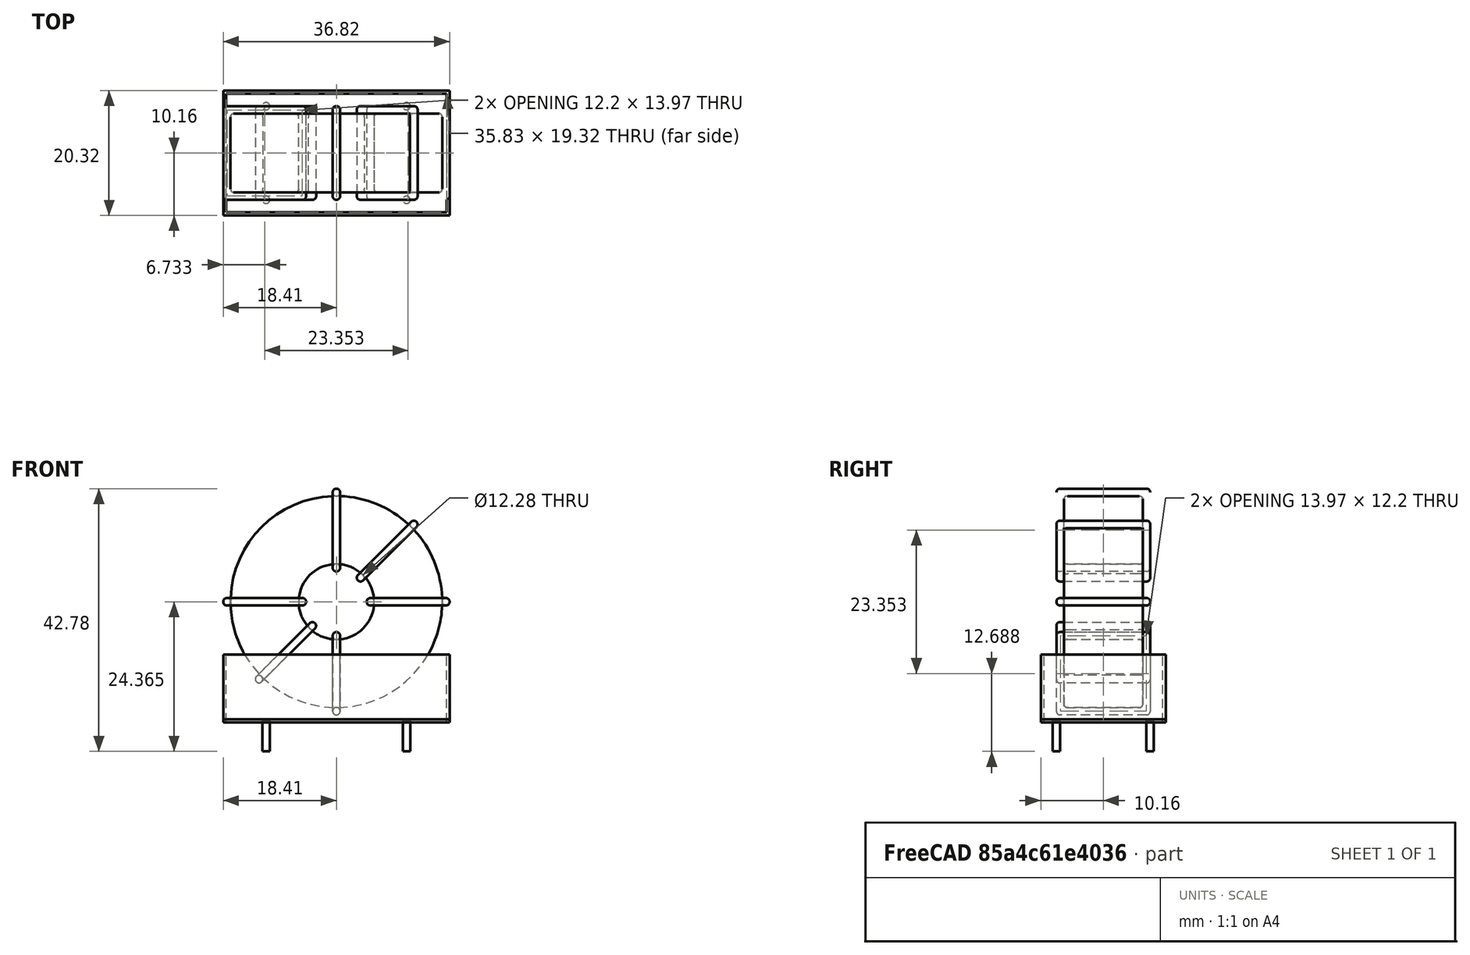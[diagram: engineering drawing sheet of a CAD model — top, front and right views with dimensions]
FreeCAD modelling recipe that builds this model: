
FCSTD DOCUMENT  (FreeCAD 0.16R6703 (Git))
Label: L_CommonModeChoke_Toroid_Vertical_L36.8mm_W20.3mm_Px15.24mm_Py22.86mm_Bourns_8100series
License: All rights reserved
LicenseURL: http://en.wikipedia.org/wiki/All_rights_reserved
objects: Sketcher::SketchObject×8, PartDesign::Pad×8, PartDesign::Fillet×5, Spreadsheet::Sheet×1
note: 29 computed .brp shape members not serialized (recipe doc carries the construction recipe); baked Part::Feature solids carry a one-line shape summary decoded from their .brp

FEATURE [Spreadsheet::Sheet] Spreadsheet  label="dimensions"
  cells = A1=Wx; B1(Wx)=36.83; C1(WW)=12.27666666666667; D1(iWx)=36.83; A2=Wy; B2(Wy)=15.24; D2(iWy)=20.32; A3=RM; B3(RMx)=15.24; C3(RMy)=22.86; A4=d_wire; B4(d_wire)=1.2; A5=H; B5(H)=31; A6=offsetx; B6(offsetx)=6.984999999999999
FEATURE [Sketcher::SketchObject] Sketch
  Placement = pos=(11.43,-7.62,0) rot=(1,0,0;1.5708rad)
  expr: Placement.Base.x = Spreadsheet.RMy / 2
  expr: Constraints[4] = Spreadsheet.WW / 2
  expr: Placement.Base.y = -Spreadsheet.RMx / 2
  expr: Constraints[0] = Spreadsheet.Wx / 2 - Spreadsheet.d_wire
  expr: Constraints[2] = Spreadsheet.Wx / 2 + Spreadsheet.d_wire + 0.5
  sketch-geometry (2):
    g0: Circle CenterX=0 CenterY=20.115 CenterZ=0 NormalX=0 NormalY=0 NormalZ=1 Radius=17.215
    g1: Circle CenterX=0 CenterY=20.115 CenterZ=0 NormalX=0 NormalY=0 NormalZ=1 Radius=6.13833
  constraints (5):
    c: Radius(g0) = 17.215
    c: DistanceX(g-1,g0) = 0
    c: DistanceY(g-1,g0) = 20.115
    c: Coincident(g1,g0)
    c: Radius(g1) = 6.13833
FEATURE [PartDesign::Pad] Pad
  Length = 12.84
  Length2 = 100
  Midplane = true
  Placement = pos=(11.43,-7.62,0) rot=(1,0,0;1.5708rad)
  Sketch = -> Sketch
  Type = 0
  expr: Length = Spreadsheet.Wy - 2 * Spreadsheet.d_wire
FEATURE [Sketcher::SketchObject] Sketch001
  Placement = pos=(0,0,0.75) rot=(0,0,1;0rad)
  expr: Constraints[4] = Spreadsheet.RMy
  expr: Constraints[2] = -Spreadsheet.RMx
  expr: Constraints[1] = Spreadsheet.d_wire / 2
  sketch-geometry (4):
    g0: Circle CenterX=0 CenterY=0 CenterZ=0 NormalX=0 NormalY=0 NormalZ=1 Radius=0.6
    g1: Circle CenterX=22.86 CenterY=-15.24 CenterZ=0 NormalX=0 NormalY=0 NormalZ=1 Radius=0.6
    g2: Circle CenterX=0 CenterY=-15.24 CenterZ=0 NormalX=0 NormalY=0 NormalZ=1 Radius=0.6
    g3: Circle CenterX=22.86 CenterY=0 CenterZ=0 NormalX=0 NormalY=0 NormalZ=1 Radius=0.6
  constraints (11):
    c: Equal(g0,g1)
    c: Radius(g0) = 0.6
    c: DistanceY(g-1,g1) = -15.24
    c: Coincident(g0,g-1)
    c: DistanceX(g-1,g1) = 22.86
    c: PointOnObject(g2,g-2)
    c: DistanceY(g-1,g3) = 0
    c: DistanceY(g2,g1) = 0
    c: DistanceX(g3,g1) = 0
    c: Equal(g3,g2)
    c: Equal(g2,g1)
FEATURE [PartDesign::Pad] Pad001
  Length = 5
  Length2 = 0
  Placement = pos=(0,0,0.75) rot=(0,0,1;0rad)
  Reversed = true
  Sketch = -> Sketch001
  Type = 0
FEATURE [PartDesign::Fillet] Fillet
  Base = -> Pad [Edge6,Edge3,Edge2]
  Placement = pos=(11.43,-7.62,0) rot=(1,0,0;1.5708rad)
  Radius = 0.5
FEATURE [Sketcher::SketchObject] Sketch003
  Placement = pos=(11.43,0,20.115) rot=(1,0,0;3.14159rad)
  expr: Placement.Base.x = Spreadsheet.RMy / 2
  expr: Constraints[18] = Spreadsheet.d_wire
  expr: Constraints[16] = Spreadsheet.d_wire
  expr: Constraints[19] = Spreadsheet.d_wire
  expr: Constraints[17] = Spreadsheet.d_wire
  expr: Placement.Base.y = -1 * (Spreadsheet.RMx - Spreadsheet.Wy) / 2
  expr: Constraints[21] = (Spreadsheet.Wx - Spreadsheet.WW) / 2 - Spreadsheet.d_wire
  expr: Constraints[22] = Spreadsheet.Wx / 2 - Spreadsheet.d_wire
  expr: Constraints[43] = Spreadsheet.d_wire
  expr: Constraints[48] = Spreadsheet.Wx - Spreadsheet.d_wire * 2
  expr: Constraints[49] = Spreadsheet.Wy
  expr: Placement.Base.z = Spreadsheet.Wx / 2 + Spreadsheet.d_wire + 0.5
  sketch-geometry (16):
    g0: LineSegment StartX=-4.93833 StartY=0 StartZ=0 EndX=-18.415 EndY=0 EndZ=0
    g1: LineSegment StartX=-18.415 StartY=0 StartZ=0 EndX=-18.415 EndY=15.24 EndZ=0
    g2: LineSegment StartX=-18.415 StartY=15.24 StartZ=0 EndX=-4.93833 EndY=15.24 EndZ=0
    g3: LineSegment StartX=-4.93833 StartY=15.24 StartZ=0 EndX=-4.93833 EndY=0 EndZ=0
    g4: LineSegment StartX=-17.215 StartY=14.04 StartZ=0 EndX=-6.13833 EndY=14.04 EndZ=0
    g5: LineSegment StartX=-6.13833 StartY=14.04 StartZ=0 EndX=-6.13833 EndY=1.2 EndZ=0
    g6: LineSegment StartX=-6.13833 StartY=1.2 StartZ=0 EndX=-17.215 EndY=1.2 EndZ=0
    g7: LineSegment StartX=-17.215 StartY=1.2 StartZ=0 EndX=-17.215 EndY=14.04 EndZ=0
    g8: LineSegment StartX=4.93833 StartY=15.24 StartZ=0 EndX=18.415 EndY=15.24 EndZ=0
    g9: LineSegment StartX=18.415 StartY=15.24 StartZ=0 EndX=18.415 EndY=0 EndZ=0
    g10: LineSegment StartX=18.415 StartY=0 StartZ=0 EndX=4.93833 EndY=0 EndZ=0
    g11: LineSegment StartX=4.93833 StartY=0 StartZ=0 EndX=4.93833 EndY=15.24 EndZ=0
    g12: LineSegment StartX=6.13833 StartY=14.04 StartZ=0 EndX=17.215 EndY=14.04 EndZ=0
    g13: LineSegment StartX=17.215 StartY=14.04 StartZ=0 EndX=17.215 EndY=1.2 EndZ=0
    g14: LineSegment StartX=17.215 StartY=1.2 StartZ=0 EndX=6.13833 EndY=1.2 EndZ=0
    g15: LineSegment StartX=6.13833 StartY=1.2 StartZ=0 EndX=6.13833 EndY=14.04 EndZ=0
  constraints (50):
    c: Horizontal(g0)
    c: Coincident(g1,g0)
    c: Vertical(g1)
    c: Coincident(g2,g1)
    c: Horizontal(g2)
    c: Coincident(g3,g2)
    c: Coincident(g3,g0)
    c: Vertical(g3)
    c: Coincident(g4,g5)
    c: Coincident(g5,g6)
    c: Coincident(g6,g7)
    c: Coincident(g7,g4)
    c: Horizontal(g4)
    c: Horizontal(g6)
    c: Vertical(g5)
    c: Vertical(g7)
    c: DistanceX(g1,g4) = 1.2
    c: DistanceY(g4,g1) = 1.2
    c: DistanceX(g5,g0) = 1.2
    c: DistanceY(g0,g5) = 1.2
    c: DistanceY(g-1,g0) = 0
    c: DistanceX(g6,g6) = 11.0767
    c: DistanceX(g6,g-1) = 17.215
    c: Coincident(g8,g9)
    c: Coincident(g9,g10)
    c: Coincident(g10,g11)
    c: Coincident(g11,g8)
    c: Horizontal(g8)
    c: Horizontal(g10)
    c: Vertical(g9)
    c: Vertical(g11)
    c: Coincident(g12,g13)
    c: Coincident(g13,g14)
    c: Coincident(g14,g15)
    c: Coincident(g15,g12)
    c: Horizontal(g12)
    c: Horizontal(g14)
    c: Vertical(g13)
    c: Vertical(g15)
    c: DistanceY(g8,g2) = 0
    c: DistanceY(g10,g0) = 0
    c: DistanceY(g14,g5) = 0
    c: DistanceY(g12,g4) = 0
    c: DistanceX(g8,g12) = 1.2
    c: Equal(g8,g2)
    c: Equal(g12,g4)
    c: Equal(g9,g1)
    c: Equal(g13,g7)
    c: DistanceX(g4,g12) = 34.43
    c: DistanceY(g0,g1) = 15.24
FEATURE [PartDesign::Pad] Pad002
  Length = 1.2
  Length2 = 100
  Midplane = true
  Placement = pos=(11.43,0,20.115) rot=(1,0,0;3.14159rad)
  Sketch = -> Sketch003
  Type = 0
  expr: Length = Spreadsheet.d_wire
FEATURE [PartDesign::Fillet] Fillet001
  Base = -> Pad002 [Edge38,Edge41,Edge42,Edge43,Edge29,Edge32,Edge33,Edge34,Edge25,Edge35,Edge36,Edge13,Edge14,Edge15,Edge16,Edge17,Edge18,Edge19,Edge1,Edge2,Edge3,Edge4,Edge5,Edge6,Edge7,Edge37,Edge39,Edge40,Edge20,Edge23,Edge24,Edge21,Edge22,Edge8,Edge9,Edge10,Edge11,Edge12,Edge26,Edge27,+8 more]
  Placement = pos=(11.43,0,20.115) rot=(1,0,0;3.14159rad)
  Radius = 0.564
  expr: Radius = Spreadsheet.d_wire * 0.47
FEATURE [Sketcher::SketchObject] Sketch004
  Placement = pos=(11.43,0,20.115) rot=(0.92388,0,0.382683;3.14159rad)
  expr: Placement.Base.x = Spreadsheet.RMy / 2
  expr: Constraints[18] = Spreadsheet.d_wire
  expr: Constraints[16] = Spreadsheet.d_wire
  expr: Constraints[19] = Spreadsheet.d_wire
  expr: Constraints[17] = Spreadsheet.d_wire
  expr: Placement.Base.y = -1 * (Spreadsheet.RMx - Spreadsheet.Wy) / 2
  expr: Constraints[21] = (Spreadsheet.Wx - Spreadsheet.WW) / 2 - Spreadsheet.d_wire
  expr: Constraints[22] = Spreadsheet.Wx / 2 - Spreadsheet.d_wire
  expr: Constraints[43] = Spreadsheet.d_wire
  expr: Constraints[48] = Spreadsheet.Wx - 2 * Spreadsheet.d_wire
  expr: Constraints[49] = Spreadsheet.Wy
  expr: Placement.Base.z = Spreadsheet.Wx / 2 + Spreadsheet.d_wire + 0.5
  sketch-geometry (16):
    g0: LineSegment StartX=-4.93833 StartY=0 StartZ=0 EndX=-18.415 EndY=0 EndZ=0
    g1: LineSegment StartX=-18.415 StartY=0 StartZ=0 EndX=-18.415 EndY=15.24 EndZ=0
    g2: LineSegment StartX=-18.415 StartY=15.24 StartZ=0 EndX=-4.93833 EndY=15.24 EndZ=0
    g3: LineSegment StartX=-4.93833 StartY=15.24 StartZ=0 EndX=-4.93833 EndY=0 EndZ=0
    g4: LineSegment StartX=-17.215 StartY=14.04 StartZ=0 EndX=-6.13833 EndY=14.04 EndZ=0
    g5: LineSegment StartX=-6.13833 StartY=14.04 StartZ=0 EndX=-6.13833 EndY=1.2 EndZ=0
    g6: LineSegment StartX=-6.13833 StartY=1.2 StartZ=0 EndX=-17.215 EndY=1.2 EndZ=0
    g7: LineSegment StartX=-17.215 StartY=1.2 StartZ=0 EndX=-17.215 EndY=14.04 EndZ=0
    g8: LineSegment StartX=4.93833 StartY=15.24 StartZ=0 EndX=18.415 EndY=15.24 EndZ=0
    g9: LineSegment StartX=18.415 StartY=15.24 StartZ=0 EndX=18.415 EndY=0 EndZ=0
    g10: LineSegment StartX=18.415 StartY=0 StartZ=0 EndX=4.93833 EndY=0 EndZ=0
    g11: LineSegment StartX=4.93833 StartY=0 StartZ=0 EndX=4.93833 EndY=15.24 EndZ=0
    g12: LineSegment StartX=6.13833 StartY=14.04 StartZ=0 EndX=17.215 EndY=14.04 EndZ=0
    g13: LineSegment StartX=17.215 StartY=14.04 StartZ=0 EndX=17.215 EndY=1.2 EndZ=0
    g14: LineSegment StartX=17.215 StartY=1.2 StartZ=0 EndX=6.13833 EndY=1.2 EndZ=0
    g15: LineSegment StartX=6.13833 StartY=1.2 StartZ=0 EndX=6.13833 EndY=14.04 EndZ=0
  constraints (50):
    c: Horizontal(g0)
    c: Coincident(g1,g0)
    c: Vertical(g1)
    c: Coincident(g2,g1)
    c: Horizontal(g2)
    c: Coincident(g3,g2)
    c: Coincident(g3,g0)
    c: Vertical(g3)
    c: Coincident(g4,g5)
    c: Coincident(g5,g6)
    c: Coincident(g6,g7)
    c: Coincident(g7,g4)
    c: Horizontal(g4)
    c: Horizontal(g6)
    c: Vertical(g5)
    c: Vertical(g7)
    c: DistanceX(g1,g4) = 1.2
    c: DistanceY(g4,g1) = 1.2
    c: DistanceX(g5,g0) = 1.2
    c: DistanceY(g0,g5) = 1.2
    c: DistanceY(g-1,g0) = 0
    c: DistanceX(g6,g6) = 11.0767
    c: DistanceX(g6,g-1) = 17.215
    c: Coincident(g8,g9)
    c: Coincident(g9,g10)
    c: Coincident(g10,g11)
    c: Coincident(g11,g8)
    c: Horizontal(g8)
    c: Horizontal(g10)
    c: Vertical(g9)
    c: Vertical(g11)
    c: Coincident(g12,g13)
    c: Coincident(g13,g14)
    c: Coincident(g14,g15)
    c: Coincident(g15,g12)
    c: Horizontal(g12)
    c: Horizontal(g14)
    c: Vertical(g13)
    c: Vertical(g15)
    c: DistanceY(g8,g2) = 0
    c: DistanceY(g10,g0) = 0
    c: DistanceY(g14,g5) = 0
    c: DistanceY(g12,g4) = 0
    c: DistanceX(g8,g12) = 1.2
    c: Equal(g8,g2)
    c: Equal(g12,g4)
    c: Equal(g9,g1)
    c: Equal(g13,g7)
    c: DistanceX(g4,g12) = 34.43
    c: DistanceY(g0,g1) = 15.24
FEATURE [PartDesign::Pad] Pad003
  Length = 1.2
  Length2 = 100
  Midplane = true
  Placement = pos=(11.43,0,20.115) rot=(0.92388,0,0.382683;3.14159rad)
  Sketch = -> Sketch004
  Type = 0
  expr: Length = Spreadsheet.d_wire
FEATURE [PartDesign::Fillet] Fillet002
  Base = -> Pad003 [Edge38,Edge41,Edge42,Edge43,Edge29,Edge32,Edge33,Edge34,Edge25,Edge35,Edge36,Edge13,Edge14,Edge15,Edge16,Edge17,Edge18,Edge19,Edge1,Edge2,Edge3,Edge4,Edge5,Edge6,Edge7,Edge37,Edge39,Edge40,Edge20,Edge23,Edge24,Edge21,Edge22,Edge8,Edge9,Edge10,Edge11,Edge12,Edge26,Edge27,+8 more]
  Placement = pos=(11.43,0,20.115) rot=(0.92388,0,0.382683;3.14159rad)
  Radius = 0.564
  expr: Radius = Spreadsheet.d_wire * 0.47
FEATURE [Sketcher::SketchObject] Sketch005
  Placement = pos=(11.43,0,20.115) rot=(0.92388,0,-0.382683;3.14159rad)
  expr: Placement.Base.x = Spreadsheet.RMy / 2
  expr: Constraints[18] = Spreadsheet.d_wire
  expr: Constraints[16] = Spreadsheet.d_wire
  expr: Constraints[19] = Spreadsheet.d_wire
  expr: Constraints[17] = Spreadsheet.d_wire
  expr: Placement.Base.y = -1 * (Spreadsheet.RMx - Spreadsheet.Wy) / 2
  expr: Constraints[21] = (Spreadsheet.Wx - Spreadsheet.WW) / 2 - Spreadsheet.d_wire
  expr: Constraints[22] = Spreadsheet.Wx / 2 - Spreadsheet.d_wire
  expr: Constraints[43] = Spreadsheet.d_wire
  expr: Constraints[48] = Spreadsheet.Wx - 2 * Spreadsheet.d_wire
  expr: Constraints[49] = Spreadsheet.Wy
  expr: Placement.Base.z = Spreadsheet.Wx / 2 + Spreadsheet.d_wire + 0.5
  sketch-geometry (16):
    g0: LineSegment StartX=-4.93833 StartY=0 StartZ=0 EndX=-18.415 EndY=0 EndZ=0
    g1: LineSegment StartX=-18.415 StartY=0 StartZ=0 EndX=-18.415 EndY=15.24 EndZ=0
    g2: LineSegment StartX=-18.415 StartY=15.24 StartZ=0 EndX=-4.93833 EndY=15.24 EndZ=0
    g3: LineSegment StartX=-4.93833 StartY=15.24 StartZ=0 EndX=-4.93833 EndY=0 EndZ=0
    g4: LineSegment StartX=-17.215 StartY=14.04 StartZ=0 EndX=-6.13833 EndY=14.04 EndZ=0
    g5: LineSegment StartX=-6.13833 StartY=14.04 StartZ=0 EndX=-6.13833 EndY=1.2 EndZ=0
    g6: LineSegment StartX=-6.13833 StartY=1.2 StartZ=0 EndX=-17.215 EndY=1.2 EndZ=0
    g7: LineSegment StartX=-17.215 StartY=1.2 StartZ=0 EndX=-17.215 EndY=14.04 EndZ=0
    g8: LineSegment StartX=4.93833 StartY=15.24 StartZ=0 EndX=18.415 EndY=15.24 EndZ=0
    g9: LineSegment StartX=18.415 StartY=15.24 StartZ=0 EndX=18.415 EndY=0 EndZ=0
    g10: LineSegment StartX=18.415 StartY=0 StartZ=0 EndX=4.93833 EndY=0 EndZ=0
    g11: LineSegment StartX=4.93833 StartY=0 StartZ=0 EndX=4.93833 EndY=15.24 EndZ=0
    g12: LineSegment StartX=6.13833 StartY=14.04 StartZ=0 EndX=17.215 EndY=14.04 EndZ=0
    g13: LineSegment StartX=17.215 StartY=14.04 StartZ=0 EndX=17.215 EndY=1.2 EndZ=0
    g14: LineSegment StartX=17.215 StartY=1.2 StartZ=0 EndX=6.13833 EndY=1.2 EndZ=0
    g15: LineSegment StartX=6.13833 StartY=1.2 StartZ=0 EndX=6.13833 EndY=14.04 EndZ=0
  constraints (50):
    c: Horizontal(g0)
    c: Coincident(g1,g0)
    c: Vertical(g1)
    c: Coincident(g2,g1)
    c: Horizontal(g2)
    c: Coincident(g3,g2)
    c: Coincident(g3,g0)
    c: Vertical(g3)
    c: Coincident(g4,g5)
    c: Coincident(g5,g6)
    c: Coincident(g6,g7)
    c: Coincident(g7,g4)
    c: Horizontal(g4)
    c: Horizontal(g6)
    c: Vertical(g5)
    c: Vertical(g7)
    c: DistanceX(g1,g4) = 1.2
    c: DistanceY(g4,g1) = 1.2
    c: DistanceX(g5,g0) = 1.2
    c: DistanceY(g0,g5) = 1.2
    c: DistanceY(g-1,g0) = 0
    c: DistanceX(g6,g6) = 11.0767
    c: DistanceX(g6,g-1) = 17.215
    c: Coincident(g8,g9)
    c: Coincident(g9,g10)
    c: Coincident(g10,g11)
    c: Coincident(g11,g8)
    c: Horizontal(g8)
    c: Horizontal(g10)
    c: Vertical(g9)
    c: Vertical(g11)
    c: Coincident(g12,g13)
    c: Coincident(g13,g14)
    c: Coincident(g14,g15)
    c: Coincident(g15,g12)
    c: Horizontal(g12)
    c: Horizontal(g14)
    c: Vertical(g13)
    c: Vertical(g15)
    c: DistanceY(g8,g2) = 0
    c: DistanceY(g10,g0) = 0
    c: DistanceY(g14,g5) = 0
    c: DistanceY(g12,g4) = 0
    c: DistanceX(g8,g12) = 1.2
    c: Equal(g8,g2)
    c: Equal(g12,g4)
    c: Equal(g9,g1)
    c: Equal(g13,g7)
    c: DistanceX(g4,g12) = 34.43
    c: DistanceY(g0,g1) = 15.24
FEATURE [PartDesign::Pad] Pad004
  Length = 1.2
  Length2 = 100
  Midplane = true
  Placement = pos=(11.43,0,20.115) rot=(0.92388,0,-0.382683;3.14159rad)
  Sketch = -> Sketch005
  Type = 0
  expr: Length = Spreadsheet.d_wire
FEATURE [PartDesign::Fillet] Fillet003
  Base = -> Pad004 [Edge38,Edge41,Edge42,Edge43,Edge29,Edge32,Edge33,Edge34,Edge25,Edge35,Edge36,Edge13,Edge14,Edge15,Edge16,Edge17,Edge18,Edge19,Edge1,Edge2,Edge3,Edge4,Edge5,Edge6,Edge7,Edge37,Edge39,Edge40,Edge20,Edge23,Edge24,Edge21,Edge22,Edge8,Edge9,Edge10,Edge11,Edge12,Edge26,Edge27,+8 more]
  Placement = pos=(11.43,0,20.115) rot=(0.92388,0,-0.382683;3.14159rad)
  Radius = 0.564
  expr: Radius = Spreadsheet.d_wire * 0.47
FEATURE [Sketcher::SketchObject] Sketch006
  Placement = pos=(11.43,0,20.115) rot=(0.707107,0,0.707107;3.14159rad)
  expr: Placement.Base.x = Spreadsheet.RMy / 2
  expr: Constraints[18] = Spreadsheet.d_wire
  expr: Constraints[16] = Spreadsheet.d_wire
  expr: Constraints[19] = Spreadsheet.d_wire
  expr: Constraints[17] = Spreadsheet.d_wire
  expr: Placement.Base.y = -1 * (Spreadsheet.RMx - Spreadsheet.Wy) / 2
  expr: Constraints[21] = (Spreadsheet.Wx - Spreadsheet.WW) / 2 - Spreadsheet.d_wire
  expr: Constraints[22] = Spreadsheet.Wx / 2 - Spreadsheet.d_wire
  expr: Constraints[43] = Spreadsheet.d_wire
  expr: Constraints[48] = Spreadsheet.Wx - Spreadsheet.d_wire * 2
  expr: Constraints[49] = Spreadsheet.Wy
  expr: Placement.Base.z = Spreadsheet.Wx / 2 + Spreadsheet.d_wire + 0.5
  sketch-geometry (16):
    g0: LineSegment StartX=-4.93833 StartY=0 StartZ=0 EndX=-18.415 EndY=0 EndZ=0
    g1: LineSegment StartX=-18.415 StartY=0 StartZ=0 EndX=-18.415 EndY=15.24 EndZ=0
    g2: LineSegment StartX=-18.415 StartY=15.24 StartZ=0 EndX=-4.93833 EndY=15.24 EndZ=0
    g3: LineSegment StartX=-4.93833 StartY=15.24 StartZ=0 EndX=-4.93833 EndY=0 EndZ=0
    g4: LineSegment StartX=-17.215 StartY=14.04 StartZ=0 EndX=-6.13833 EndY=14.04 EndZ=0
    g5: LineSegment StartX=-6.13833 StartY=14.04 StartZ=0 EndX=-6.13833 EndY=1.2 EndZ=0
    g6: LineSegment StartX=-6.13833 StartY=1.2 StartZ=0 EndX=-17.215 EndY=1.2 EndZ=0
    g7: LineSegment StartX=-17.215 StartY=1.2 StartZ=0 EndX=-17.215 EndY=14.04 EndZ=0
    g8: LineSegment StartX=4.93833 StartY=15.24 StartZ=0 EndX=18.415 EndY=15.24 EndZ=0
    g9: LineSegment StartX=18.415 StartY=15.24 StartZ=0 EndX=18.415 EndY=0 EndZ=0
    g10: LineSegment StartX=18.415 StartY=0 StartZ=0 EndX=4.93833 EndY=0 EndZ=0
    g11: LineSegment StartX=4.93833 StartY=0 StartZ=0 EndX=4.93833 EndY=15.24 EndZ=0
    g12: LineSegment StartX=6.13833 StartY=14.04 StartZ=0 EndX=17.215 EndY=14.04 EndZ=0
    g13: LineSegment StartX=17.215 StartY=14.04 StartZ=0 EndX=17.215 EndY=1.2 EndZ=0
    g14: LineSegment StartX=17.215 StartY=1.2 StartZ=0 EndX=6.13833 EndY=1.2 EndZ=0
    g15: LineSegment StartX=6.13833 StartY=1.2 StartZ=0 EndX=6.13833 EndY=14.04 EndZ=0
  constraints (50):
    c: Horizontal(g0)
    c: Coincident(g1,g0)
    c: Vertical(g1)
    c: Coincident(g2,g1)
    c: Horizontal(g2)
    c: Coincident(g3,g2)
    c: Coincident(g3,g0)
    c: Vertical(g3)
    c: Coincident(g4,g5)
    c: Coincident(g5,g6)
    c: Coincident(g6,g7)
    c: Coincident(g7,g4)
    c: Horizontal(g4)
    c: Horizontal(g6)
    c: Vertical(g5)
    c: Vertical(g7)
    c: DistanceX(g1,g4) = 1.2
    c: DistanceY(g4,g1) = 1.2
    c: DistanceX(g5,g0) = 1.2
    c: DistanceY(g0,g5) = 1.2
    c: DistanceY(g-1,g0) = 0
    c: DistanceX(g6,g6) = 11.0767
    c: DistanceX(g6,g-1) = 17.215
    c: Coincident(g8,g9)
    c: Coincident(g9,g10)
    c: Coincident(g10,g11)
    c: Coincident(g11,g8)
    c: Horizontal(g8)
    c: Horizontal(g10)
    c: Vertical(g9)
    c: Vertical(g11)
    c: Coincident(g12,g13)
    c: Coincident(g13,g14)
    c: Coincident(g14,g15)
    c: Coincident(g15,g12)
    c: Horizontal(g12)
    c: Horizontal(g14)
    c: Vertical(g13)
    c: Vertical(g15)
    c: DistanceY(g8,g2) = 0
    c: DistanceY(g10,g0) = 0
    c: DistanceY(g14,g5) = 0
    c: DistanceY(g12,g4) = 0
    c: DistanceX(g8,g12) = 1.2
    c: Equal(g8,g2)
    c: Equal(g12,g4)
    c: Equal(g9,g1)
    c: Equal(g13,g7)
    c: DistanceX(g4,g12) = 34.43
    c: DistanceY(g0,g1) = 15.24
FEATURE [PartDesign::Pad] Pad005
  Length = 1.2
  Length2 = 100
  Midplane = true
  Placement = pos=(11.43,0,20.115) rot=(0.707107,0,0.707107;3.14159rad)
  Sketch = -> Sketch006
  Type = 0
  expr: Length = Spreadsheet.d_wire
FEATURE [PartDesign::Fillet] Fillet004
  Base = -> Pad005 [Edge38,Edge41,Edge42,Edge43,Edge29,Edge32,Edge33,Edge34,Edge25,Edge35,Edge36,Edge13,Edge14,Edge15,Edge16,Edge17,Edge18,Edge19,Edge1,Edge2,Edge3,Edge4,Edge5,Edge6,Edge7,Edge37,Edge39,Edge40,Edge20,Edge23,Edge24,Edge21,Edge22,Edge8,Edge9,Edge10,Edge11,Edge12,Edge26,Edge27,+8 more]
  Placement = pos=(11.43,0,20.115) rot=(0.707107,0,0.707107;3.14159rad)
  Radius = 0.564
  expr: Radius = Spreadsheet.d_wire * 0.47
FEATURE [Sketcher::SketchObject] Sketch007
  Placement = pos=(11.43,0,0.5) rot=(0,0,1;0rad)
  expr: Placement.Base.x = Spreadsheet.RMy / 2
  expr: Placement.Base.z = 0.5
  expr: Constraints[11] = Spreadsheet.iWx / 2
  expr: Constraints[10] = (Spreadsheet.iWy - Spreadsheet.RMx) / 2
  expr: Constraints[9] = Spreadsheet.iWy
  expr: Constraints[8] = Spreadsheet.iWx
  sketch-geometry (4):
    g0: LineSegment StartX=-18.415 StartY=2.54 StartZ=0 EndX=18.415 EndY=2.54 EndZ=0
    g1: LineSegment StartX=18.415 StartY=2.54 StartZ=0 EndX=18.415 EndY=-17.78 EndZ=0
    g2: LineSegment StartX=18.415 StartY=-17.78 StartZ=0 EndX=-18.415 EndY=-17.78 EndZ=0
    g3: LineSegment StartX=-18.415 StartY=-17.78 StartZ=0 EndX=-18.415 EndY=2.54 EndZ=0
  constraints (12):
    c: Coincident(g0,g1)
    c: Coincident(g1,g2)
    c: Coincident(g2,g3)
    c: Coincident(g3,g0)
    c: Horizontal(g0)
    c: Horizontal(g2)
    c: Vertical(g1)
    c: Vertical(g3)
    c: DistanceX(g0,g0) = 36.83
    c: DistanceY(g3,g3) = 20.32
    c: DistanceY(g-1,g0) = 2.54
    c: DistanceX(g0,g-1) = 18.415
FEATURE [PartDesign::Pad] Pad006
  Length = 0.5
  Length2 = 100
  Placement = pos=(11.43,0,0.5) rot=(0,0,1;0rad)
  Sketch = -> Sketch007
  Type = 0
FEATURE [Sketcher::SketchObject] Sketch008
  Placement = pos=(11.43,0,0.5) rot=(0,0,1;0rad)
  expr: Placement.Base.x = Spreadsheet.RMy / 2
  expr: Constraints[8] = Spreadsheet.iWx
  expr: Constraints[9] = Spreadsheet.iWy
  expr: Constraints[10] = (Spreadsheet.iWy - Spreadsheet.RMx) / 2
  expr: Placement.Base.z = 0.5
  expr: Constraints[21] = 0.5
  expr: Constraints[11] = Spreadsheet.iWx / 2
  sketch-geometry (8):
    g0: LineSegment StartX=-18.415 StartY=2.54 StartZ=0 EndX=18.415 EndY=2.54 EndZ=0
    g1: LineSegment StartX=18.415 StartY=2.54 StartZ=0 EndX=18.415 EndY=-17.78 EndZ=0
    g2: LineSegment StartX=18.415 StartY=-17.78 StartZ=0 EndX=-18.415 EndY=-17.78 EndZ=0
    g3: LineSegment StartX=-18.415 StartY=-17.78 StartZ=0 EndX=-18.415 EndY=2.54 EndZ=0
    g4: LineSegment StartX=-17.915 StartY=2.04 StartZ=0 EndX=17.915 EndY=2.04 EndZ=0
    g5: LineSegment StartX=17.915 StartY=2.04 StartZ=0 EndX=17.915 EndY=-17.28 EndZ=0
    g6: LineSegment StartX=17.915 StartY=-17.28 StartZ=0 EndX=-17.915 EndY=-17.28 EndZ=0
    g7: LineSegment StartX=-17.915 StartY=-17.28 StartZ=0 EndX=-17.915 EndY=2.04 EndZ=0
  constraints (24):
    c: Coincident(g0,g1)
    c: Coincident(g1,g2)
    c: Coincident(g2,g3)
    c: Coincident(g3,g0)
    c: Horizontal(g0)
    c: Horizontal(g2)
    c: Vertical(g1)
    c: Vertical(g3)
    c: DistanceX(g0,g0) = 36.83
    c: DistanceY(g3,g3) = 20.32
    c: DistanceY(g-1,g0) = 2.54
    c: DistanceX(g0,g-1) = 18.415
    c: Coincident(g4,g5)
    c: Coincident(g5,g6)
    c: Coincident(g6,g7)
    c: Coincident(g7,g4)
    c: Horizontal(g4)
    c: Horizontal(g6)
    c: Vertical(g5)
    c: Vertical(g7)
    c: DistanceX(g5,g1) = 0.5
    c: DistanceY(g1,g5) = 0.5
    c: DistanceX(g0,g4) = 0.5
    c: DistanceY(g4,g0) = 0.5
FEATURE [PartDesign::Pad] Pad007
  Length = 11.049
  Length2 = 100
  Placement = pos=(11.43,0,0.5) rot=(0,0,1;0rad)
  Sketch = -> Sketch008
  Type = 0
  expr: Length = Spreadsheet.Wx * 0.3
